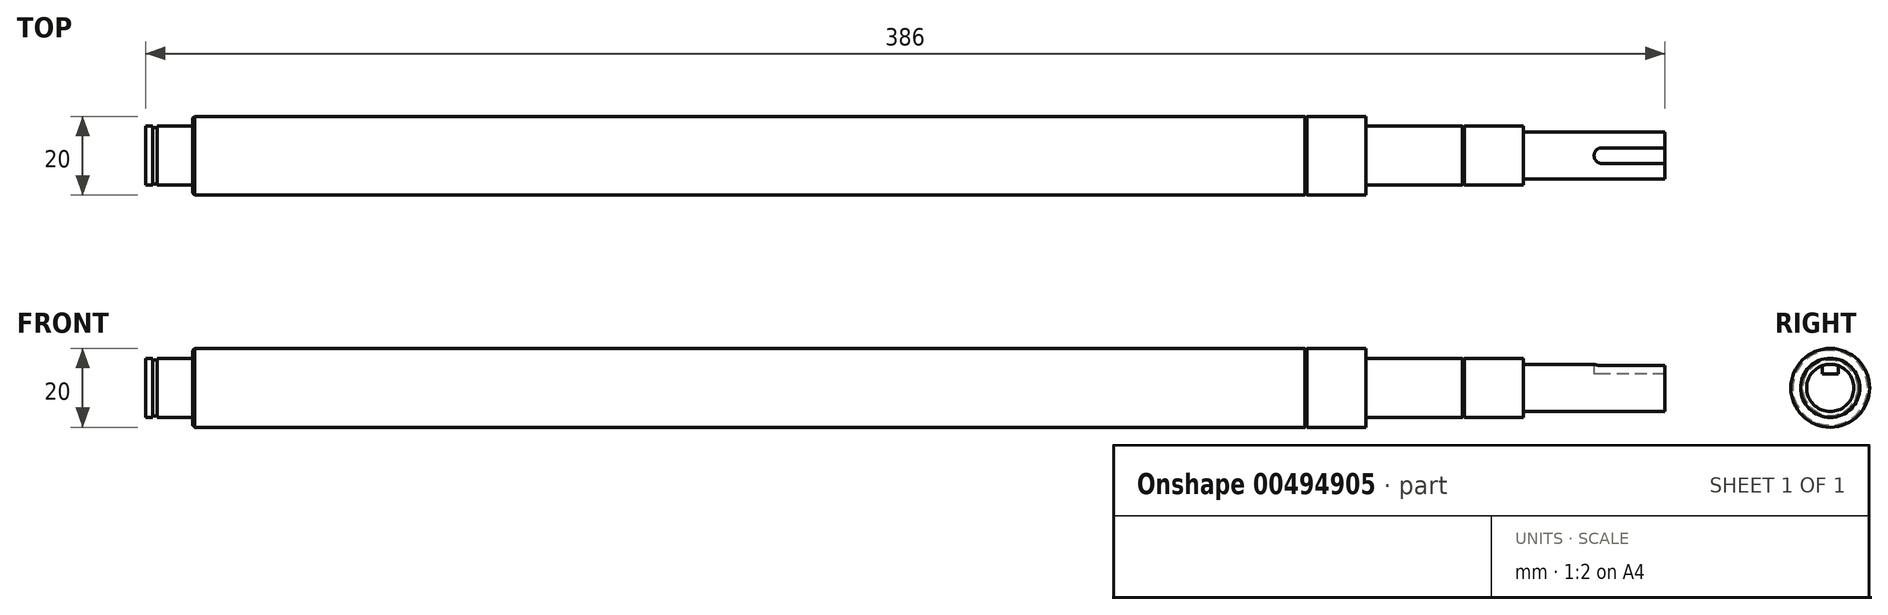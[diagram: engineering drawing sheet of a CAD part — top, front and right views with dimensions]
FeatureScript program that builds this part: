
annotation { "Feature Type Name" : "Feature", "Feature Type Description" : "" }
export const myFeature = defineFeature(function(context is Context, id is Id, definition is map)
    precondition{}
    {
        {
            var Q0;
            Q0=qCreatedBy(makeId("Right.planeOp"),FACE);
            var sketch = newSketch(context, id + "F0", { "sketchPlane" : qUnion([Q0])});
            skCircle(sketch, "E0", {"center": v(0, 0) * mm, "radius": 7.5 * mm});
            skSolve(sketch);
        }
        {
            var Q0;
            Q0=qSketchRegion(id+"F0",true);
            extrude(context, id + "F1", {"entities" : qUnion([Q0]), "oppositeDirection" : true, "depth" : 9 * mm});
        }
        {
            var Q0;
            Q0=makeQuery(id+"F1.opExtrude","CAP_FACE",FACE,{"disambiguationData":[OSD([sQuery(id+"F0.wireOp",EDGE,"E0")])],"isStart":false});
            var sketch = newSketch(context, id + "F2", { "sketchPlane" : qUnion([Q0])});
            skCircle(sketch, "E1", {"center": v(0, 0) * mm, "radius": 7.15 * mm});
            skSolve(sketch);
        }
        {
            var Q0;
            Q0=qSketchRegion(id+"F2",true);
            extrude(context, id + "F3", {"entities" : qUnion([Q0]), "operationType" : NewBodyOperationType.ADD, "depth" : 1.15 * mm});
        }
        {
            var Q0;
            Q0=makeQuery(id+"F3.opExtrude","CAP_FACE",FACE,{"disambiguationData":[OSD([sQuery(id+"F2.wireOp",EDGE,"E1")])],"isStart":false});
            var sketch = newSketch(context, id + "F4", { "sketchPlane" : qUnion([Q0])});
            skCircle(sketch, "E2", {"center": v(0, 0) * mm, "radius": 7.5 * mm});
            skSolve(sketch);
        }
        {
            var Q0;
            Q0=qSketchRegion(id+"F4",true);
            extrude(context, id + "F5", {"entities" : qUnion([Q0]), "operationType" : NewBodyOperationType.ADD, "depth" : 1.85 * mm});
        }
        {
            var Q0;
            Q0=qCreatedBy(makeId("Right.planeOp"),FACE);
            var sketch = newSketch(context, id + "F6", { "sketchPlane" : qUnion([Q0])});
            skCircle(sketch, "E3", {"center": v(0, 0) * mm, "radius": 10 * mm});
            skSolve(sketch);
        }
        {
            var Q0;
            Q0=qSketchRegion(id+"F6",true);
            extrude(context, id + "F7", {"entities" : qUnion([Q0]), "operationType" : NewBodyOperationType.ADD, "depth" : 283 * mm});
        }
        {
            var Q0;
            Q0=makeQuery(id+"F7.opExtrude","CAP_EDGE",EDGE,{"disambiguationData":[OSD([sQuery(id+"F6.wireOp",EDGE,"E3")])],"isStart":false});
            var Q1;
            Q1=makeQuery(id+"F7.opExtrude","CAP_EDGE",EDGE,{"disambiguationData":[OSD([sQuery(id+"F6.wireOp",EDGE,"E3")])],"isStart":true});
            chamfer(context, id + "F8", {"entities" : qUnion([Q0, Q1]), "width" : 0.5 * mm, "tangentPropagation" : true});
        }
        {
            var Q0;
            Q0=makeQuery(id+"F7.opExtrude","CAP_FACE",FACE,{"disambiguationData":[OSD([sQuery(id+"F6.wireOp",EDGE,"E3")])],"isStart":false});
            var sketch = newSketch(context, id + "F9", { "sketchPlane" : qUnion([Q0])});
            skCircle(sketch, "E4", {"center": v(0, 0) * mm, "radius": 10 * mm});
            skSolve(sketch);
        }
        {
            var Q0;
            Q0=qSketchRegion(id+"F9",true);
            extrude(context, id + "F10", {"entities" : qUnion([Q0]), "operationType" : NewBodyOperationType.ADD, "depth" : 15 * mm});
        }
        {
            var Q0;
            Q0=makeQuery(id+"F10.opExtrude","CAP_FACE",FACE,{"disambiguationData":[OSD([sQuery(id+"F9.wireOp",EDGE,"E4")])],"isStart":false});
            var sketch = newSketch(context, id + "F11", { "sketchPlane" : qUnion([Q0])});
            skCircle(sketch, "E5", {"center": v(0, 0) * mm, "radius": 7.5 * mm});
            skSolve(sketch);
        }
        {
            var Q0;
            Q0=qSketchRegion(id+"F11",true);
            extrude(context, id + "F12", {"entities" : qUnion([Q0]), "operationType" : NewBodyOperationType.ADD, "depth" : 25 * mm});
        }
        {
            var Q0;
            Q0=makeQuery(id+"F12.opExtrude","CAP_EDGE",EDGE,{"disambiguationData":[OSD([sQuery(id+"F11.wireOp",EDGE,"E5")])],"isStart":false});
            chamfer(context, id + "F13", {"entities" : qUnion([Q0]), "width" : 0.5 * mm, "tangentPropagation" : true});
        }
        {
            var Q0;
            Q0=makeQuery(id+"F12.opExtrude","CAP_FACE",FACE,{"disambiguationData":[OSD([sQuery(id+"F11.wireOp",EDGE,"E5")])],"isStart":false});
            var sketch = newSketch(context, id + "F14", { "sketchPlane" : qUnion([Q0])});
            skCircle(sketch, "E6", {"center": v(0, 0) * mm, "radius": 7.5 * mm});
            skSolve(sketch);
        }
        {
            var Q0;
            Q0=qSketchRegion(id+"F14",true);
            extrude(context, id + "F15", {"entities" : qUnion([Q0]), "operationType" : NewBodyOperationType.ADD, "depth" : 15 * mm});
        }
        {
            var Q0;
            Q0=makeQuery(id+"F15.opExtrude","CAP_FACE",FACE,{"disambiguationData":[OSD([sQuery(id+"F14.wireOp",EDGE,"E6")])],"isStart":false});
            var sketch = newSketch(context, id + "F16", { "sketchPlane" : qUnion([Q0])});
            skCircle(sketch, "E7", {"center": v(0, 0) * mm, "radius": 6 * mm});
            skSolve(sketch);
        }
        {
            var Q0;
            Q0=qSketchRegion(id+"F16",true);
            extrude(context, id + "F17", {"entities" : qUnion([Q0]), "operationType" : NewBodyOperationType.ADD, "depth" : 36 * mm});
        }
        {
            var Q0;
            Q0=qCreatedBy(makeId("Top.planeOp"),FACE);
            cPlane(context, id + "F18", {"entities" : qUnion([Q0]), "cplaneType" : CPlaneType.OFFSET, "offset" : 6 * mm, "width" : 150 * mm, "height" : 150 * mm});
        }
        {
            var Q0;
            Q0=qCreatedBy(id+"F18.planeOp",FACE);
            var sketch = newSketch(context, id + "F19", { "sketchPlane" : qUnion([Q0])});
            skLineSegment(sketch, "E8.bottom", {"start": v(374, 2) * mm, "end": v(356, 2) * mm});
            skLineSegment(sketch, "E8.top", {"start": v(374, -2) * mm, "end": v(356, -2) * mm});
            skLineSegment(sketch, "E8.left", {"start": v(374, 2) * mm, "end": v(374, -2) * mm});
            skLineSegment(sketch, "E8.right", {"start": v(356, 2) * mm, "end": v(356, -2) * mm});
            skSolve(sketch);
        }
        {
            var Q0;
            Q0=qSketchRegion(id+"F19",true);
            extrude(context, id + "F20", {"entities" : qUnion([Q0]), "operationType" : NewBodyOperationType.REMOVE, "oppositeDirection" : true, "depth" : 2.5 * mm});
        }
        {
            var Q0;
            Q0=makeQuery(id+"F20.boolean.opBoolean","COPY",EDGE,{"derivedFrom":makeQuery(id+"F20.opExtrude","SWEPT_EDGE",EDGE,{"disambiguationData":[OSD([sQuery(id+"F19.wireOp",EDGE,"E8.bottom"),sQuery(id+"F19.wireOp",EDGE,"E8.right")])]})});
            var Q1;
            Q1=makeQuery(id+"F20.boolean.opBoolean","COPY",EDGE,{"derivedFrom":makeQuery(id+"F20.opExtrude","SWEPT_EDGE",EDGE,{"disambiguationData":[OSD([sQuery(id+"F19.wireOp",EDGE,"E8.top"),sQuery(id+"F19.wireOp",EDGE,"E8.right")])]})});
            fillet(context, id + "F21", {"entities" : qUnion([Q0, Q1]), "radius" : 2 * mm, "tangentPropagation" : true, "allowEdgeOverflow" : false});
        }
    });
